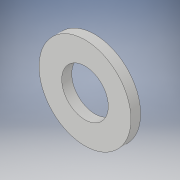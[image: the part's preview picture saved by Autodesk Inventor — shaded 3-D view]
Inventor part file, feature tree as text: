
AUTODESK INVENTOR PART (.ipt)
format: ipt  version: 2019 (Build 230136000, 136)  size: 164,352 bytes
history: native  units: mm
features: sketch x2, extrude x1, revolve x1
ambient origin geometry x8: Origin, YZ Plane, XZ Plane, XY Plane, X Axis, Y Axis, Z Axis, Center Point
bodies: Solid1 (feature_tree)
feature tree (4):
  extrude  "Extrusion1"  Depth=276.0mm
  revolve  "Revolution3"  [1 undecoded]
  sketch  "Sketch2"  dims[d1=140.0mm d2=276.0mm]
  sketch  "Sketch5"  dims[d3=30.0mm d4=0.0mm d31=41.5mm d32=11.0mm d33=23.784442mm d34=5.0mm d35=10.0mm d36=3.0mm d37=10.0mm d38=5.0mm d39=10.0mm d40=3.0mm d41=10.0mm d42=5.0mm d43=10.0mm d44=90.0deg]
note: 1 required parameter value undecoded (feature->parameter linkage not recoverable at this tier; creation-order binding heuristic only, values carry confidence <= 0.55)
